# Revit family: NLRS_57_DUA_UN_round-cooler-ac_rr-LT_sacs
name_source: partatom
category: Duct Accessories
units: mm (PartAtom-declared; Revit-internal decimal feet)

## family parameters
Always vertical = Yes
Cut with Voids When Loaded = No
OmniClass Number = 23.75.10.24.21
OmniClass Title = Cooling and Freeze Components
Part Type = Breaks Into
Round Connector Dimension = Use Diameter
Shared = No
Work Plane-Based = No

## types (1)
- AC_RR cooler
    Article_Data = AC-RR_Data
    Assembly Code = 57.00
    Cost = 0 $
    Description = Cooling battery AC_RR - Round connector - Solid Air
    IfcDescription = Cooling battery AC_RR - Round connector - Solid Air
    IfcExportAs = IfcHeatExchanger
    IfcExportType = Cooler
    Manufacturer = Solid Air Climate Solutions
    Model = AC_RR
    NLRS_C_content_datum_uitgifte = 05-07-2022
    NLRS_C_content_provider = Solid Air Climate Solutions
    NLRS_C_content_versie = 3.19.00
    NLRS_C_description = Cooling battery AC_RR - Round connector - Solid Air
    NLRS_C_niveau ontwikkeling = LOD 400
    Type Comments = Check flow directions!
    URL = https://solid-air.nl

## geometry (parser evidence)
native form markers: Sweep x9
no freeform markers — native parametric forms only
